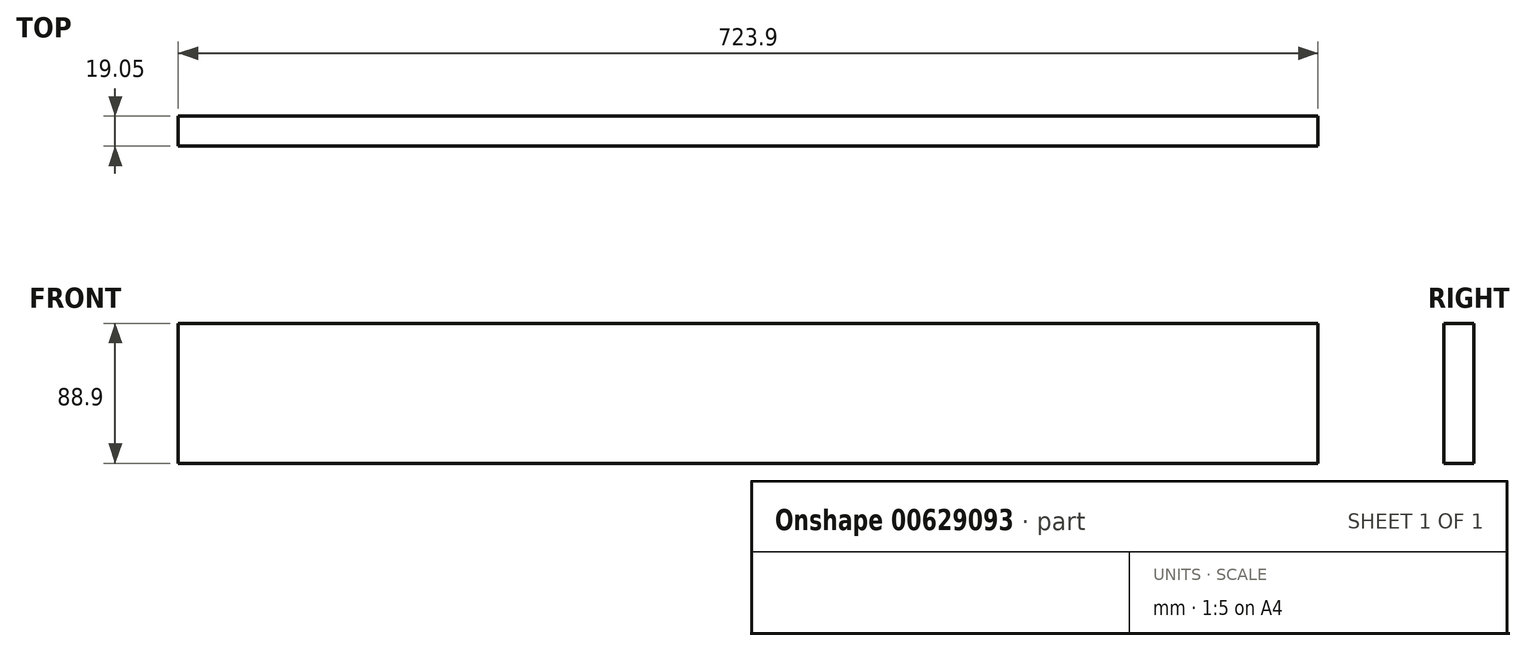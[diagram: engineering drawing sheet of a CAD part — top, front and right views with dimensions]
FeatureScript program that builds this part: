
annotation { "Feature Type Name" : "Feature", "Feature Type Description" : "" }
export const myFeature = defineFeature(function(context is Context, id is Id, definition is map)
    precondition{}
    {
        {
            var Q0;
            Q0=qCreatedBy(makeId("Front.planeOp"),FACE);
            var sketch = newSketch(context, id + "F0", { "sketchPlane" : qUnion([Q0])});
            skLineSegment(sketch, "E0.bottom", {"start": v(361.95, 44.45) * mm, "end": v(-361.95, 44.45) * mm});
            skLineSegment(sketch, "E0.top", {"start": v(361.95, -44.45) * mm, "end": v(-361.95, -44.45) * mm});
            skLineSegment(sketch, "E0.left", {"start": v(361.95, 44.45) * mm, "end": v(361.95, -44.45) * mm});
            skLineSegment(sketch, "E0.right", {"start": v(-361.95, 44.45) * mm, "end": v(-361.95, -44.45) * mm});
            skPoint(sketch, "E0.middle", {"position": v(0, 0) * mm});
            skSolve(sketch);
        }
        {
            var Q0;
            Q0=makeQuery(id+"F0.imprint","IMPRINT",FACE,{"disambiguationData":[TD([[makeQuery(id+"F0.imprint","IMPRINT",EDGE,{"derivedFrom":sQuery(id+"F0.wireOp",EDGE,"E0.bottom")}),1.0]])]});
            extrude(context, id + "F1", {"entities" : qUnion([Q0]), "depth" : 19.05 * mm, "offsetDistance" : 25.4 * mm});
        }
    });
